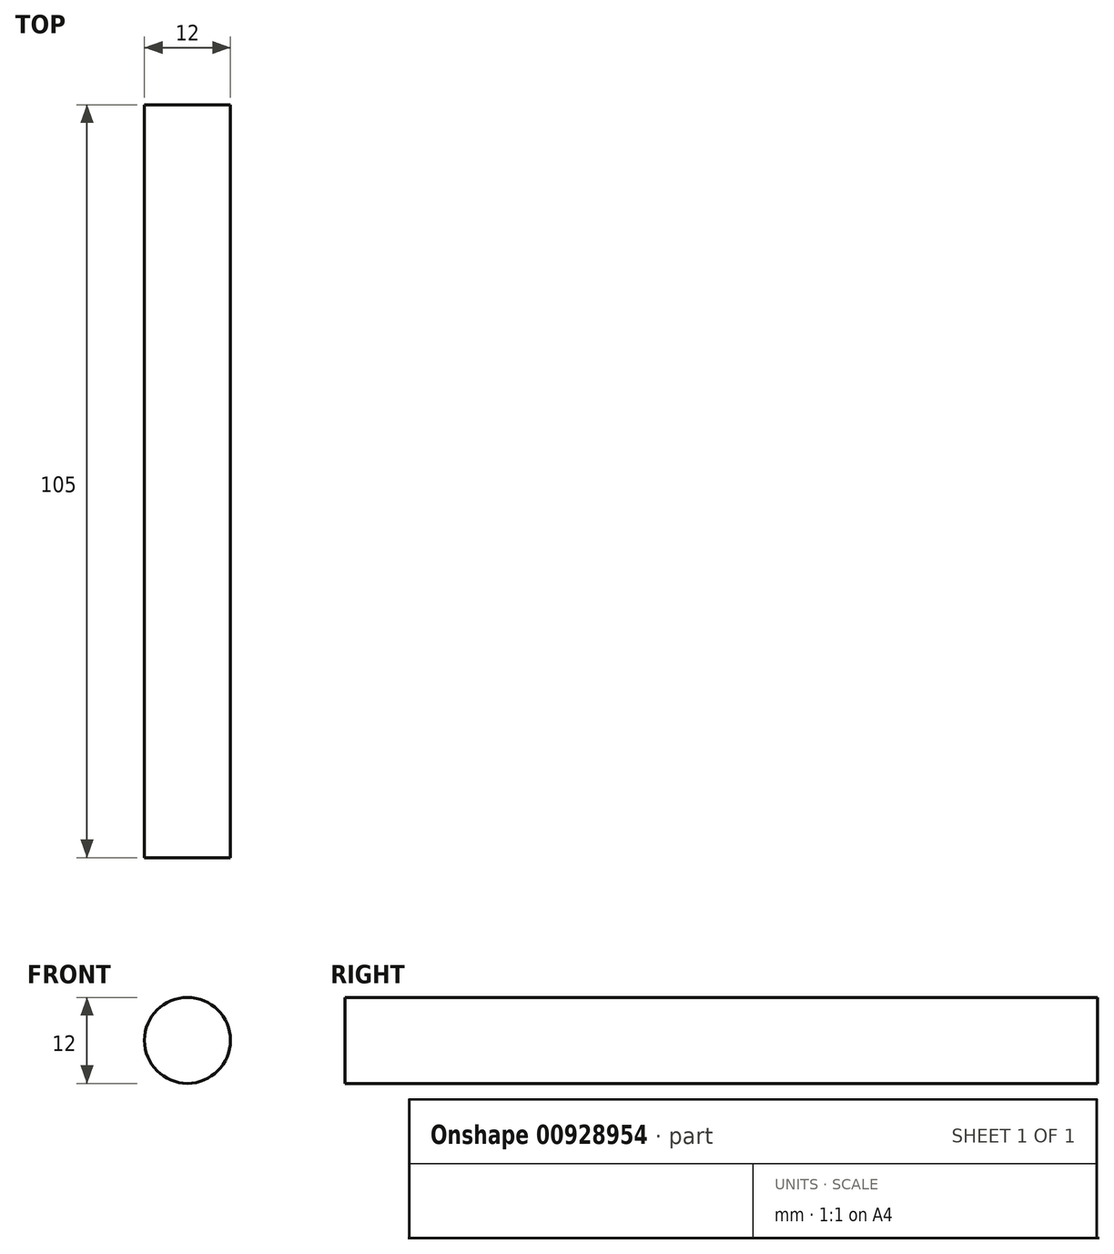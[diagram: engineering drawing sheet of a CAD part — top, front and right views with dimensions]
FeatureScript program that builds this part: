
annotation { "Feature Type Name" : "Feature", "Feature Type Description" : "" }
export const myFeature = defineFeature(function(context is Context, id is Id, definition is map)
    precondition{}
    {
        {
            var Q0;
            Q0=qCreatedBy(makeId("Front.planeOp"),FACE);
            var sketch = newSketch(context, id + "F0", { "sketchPlane" : qUnion([Q0])});
            skCircle(sketch, "E0", {"center": v(0, 0) * mm, "radius": 6 * mm});
            skSolve(sketch);
        }
        {
            var Q0;
            Q0 = qSketchRegion(id + "F0", true);
            extrude(context, id + "F1", {"entities" : qUnion([Q0]), "depth" : 105 * mm, "offsetDistance" : 25.4 * mm});
        }
    });
